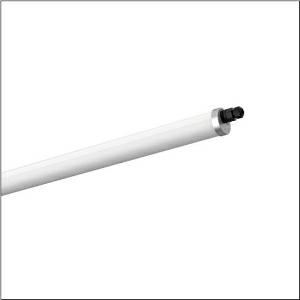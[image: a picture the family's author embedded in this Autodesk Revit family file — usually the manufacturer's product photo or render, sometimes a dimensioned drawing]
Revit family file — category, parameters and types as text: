
# Revit family: monsun_r__31_tube_51ft10dn480a_9fe9
name_source: partatom
category: Lighting Fixtures
units: mm (PartAtom-declared; Revit-internal decimal feet)

## family parameters
Cut with Voids When Loaded = No
Host = Face
Light Source = No
Part Type = Normal
Room Calculation Point = No
Round Connector Dimension = Use Diameter
Shared = No

## types (1)
- Monsun® 31 Tube (1 x LED, 8000 lm, 50 W, 4000K)
    Apparent Load = 50 VA
    CIE Flux Codes = 42 71 89 91 100
    Color Rendering = 80
    Color Temperature = 4000K
    Default Elevation = 1800 mm
    Description = Monsun® 31 Tube, tubular luminaire, primary optical cover: diffuser, of PMMA, light emission: direct distribution, primary light characteristic: symmetric, installation type: suspended mounting, surface-mounted, LED, rated luminous flux: 8.000lm, luminous efficacy: 160lm/W, light colour: 840, colour temperature: 4000K, control gear: DALI 2, with with 1 terminal, 5-pole, max. 2.5mm², through-wiring: 5x 1.5mm², mains connection: 220..240V, AC, 50/60Hz, rated input power: 50W, housing, cylindrical, of PMMA, semi-transparent, matt white, with luminaire and ceiling fastening, V4A, mounting with brackets of stainless steel, length: 1.570mm, diameter: 75mm, end cap, of stainless steel (V4A), protection rating (complete): IP67/IP69K, insulation class (complete): insulation class I (protective earthing), certification: CE, UKCA, impact resistance: IK07, permissible operating ambient temperature: -20..+40°C, corresponds to IFS (International Featured Standards) requirements for safety and quality in the food industry, usage in unprotected outdoor areas possible with horizontal mounting, contact your sales advisor before using the luminaires in applications with unclear chemical exposure, large temperature fluctuations or condensation-forming humidity, packaging unit: 1 piece
    Height = 83 mm
    Lamp = 1 x LED
    Lamp Light Flux = 8000 lm
    Lamp Power = 50 W
    Lamp count = 1
    Length = 1570 mm
    Luminous efficacy = 160 lm/W
    Manufacturer = Siteco
    ModVariant = No
    Model = 51FT10DN480A
    Mounting Place = Ceiling
    Mounting Type = Pendant
    Number of Poles = 1
    OnlyDefault = Yes
    Power Factor = 1
    Product Name = Monsun® 31 Tube
    Product group = tubular luminaire
    ProductGroupID = 906
    Protection Class = Protection class I
    RLX_Detail_Level = 1
    RLX_Emergency_Light_Flux = 0 lm
    RLX_Emergency_Type = 0
    RLX_Emergency_Type_DB = No
    RlxData = <blob elided: 25341 chars, md5=8bad1809>
    Socket = socket
    Standby Power = 0 W
    System Light Flux = 8000 lm
    System Power = 50 W
    Type Comments = Product without accessories
    Type Image = l_1228461.jpg
    URL = http://relux.com
    VarID = ---
    Voltage = 0 V
    Weight = 0.00 kg
    Width = 75 mm

## geometry (parser evidence)
native form markers: Blend x4, Sweep x14
no freeform markers — native parametric forms only
